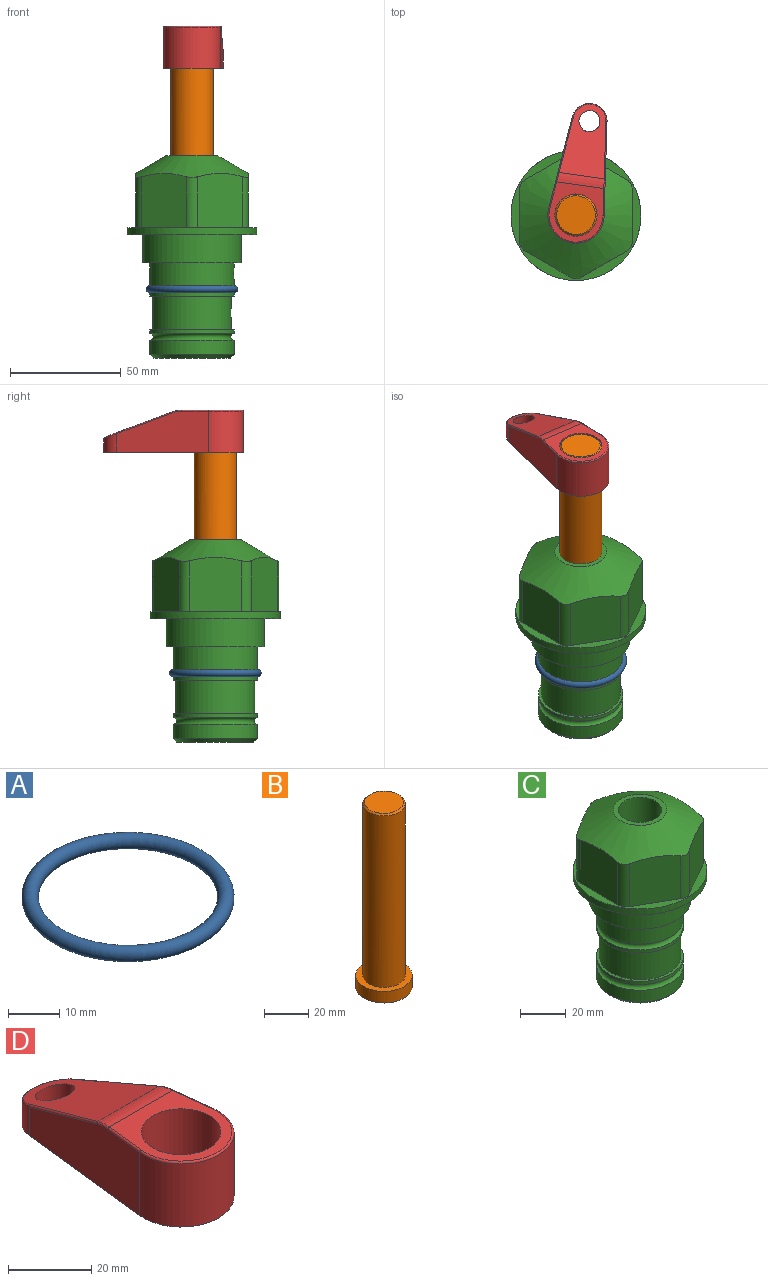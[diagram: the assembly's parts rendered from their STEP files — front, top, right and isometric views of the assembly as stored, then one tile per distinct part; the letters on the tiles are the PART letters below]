
ASSEMBLY  parts=4 mates=2
PART A: 1 faces, bbox 44.7x44.7x3.2 mm
  f0: torus R=19.05mm, axis (0,0,1), area 1193.9mm2
PART B: 6 faces, bbox 25.4x25.4x101.6 mm
  f0: plane 17.46x17.46mm, normal (0,0,1), area 239.5mm2, adj f5
  f1: plane 25.4x25.4mm, normal (0,0,-1), area 506.7mm2, adj f2
  f2: cylinder r=12.7mm len=25.4mm, axis (0,0,1), area 506.7mm2, adj f1,f3
  f3: plane 25.4x25.4mm, normal (0,0,1), area 221.7mm2, adj f2,f4
  f4: cylinder r=9.53mm len=94.46mm, axis (0,0,1), area 5653mm2, adj f3,f5
  f5: cone r=8.73mm half-angle=45deg, axis (0,0,-1), area 64.4mm2, adj f0,f4
PART C: 36 faces, bbox 58.7x58.7x91.2 mm
  f0: cylinder r=17.78mm len=35.56mm, axis (0,0,1), area 1670.8mm2, adj f23,f24,f31
  f1: cylinder r=19.05mm len=38.1mm, axis (0,0,1), area 1191.9mm2, adj f26,f27,f30
  f2: plane 58.66x58.66mm, normal (0,0,-1), area 1150.6mm2, adj f3,f28
  f3: cylinder r=29.33mm len=58.66mm, axis (0,0,-1), area 585.1mm2, adj f2,f4
  f4: plane 58.66x58.66mm, normal (0,0,1), area 475.9mm2, adj f3,f5,f6,f7,f8,f9,f10,f11
  f5: plane 24.5x20.32mm, normal (-0.5,0.87,0), area 562.8mm2, adj f4,f15,f16,f17
  f6: plane 24.5x20.32mm, normal (0.5,0.87,0), area 562.8mm2, adj f4,f14,f15,f17
  f7: plane 24.5x23.48mm, normal (1,0,0), area 562.8mm2, adj f4,f13,f14,f17
  f8: plane 24.5x20.32mm, normal (0.5,-0.87,0), area 562.8mm2, adj f4,f12,f13,f17
  f9: plane 24.5x20.32mm, normal (-0.5,-0.87,0), area 562.8mm2, adj f4,f11,f12,f17
  f10: plane 24.5x23.48mm, normal (-1,0,0), area 562.8mm2, adj f4,f11,f16,f17
  f11: cylinder r=5.08mm len=23.01mm, axis (0,0,-1), area 121.2mm2, adj f4,f9,f10,f17
  f12: cylinder r=5.08mm len=23.01mm, axis (0,0,-1), area 121.2mm2, adj f4,f8,f9,f17
  f13: cylinder r=5.08mm len=23.01mm, axis (0,0,-1), area 121.2mm2, adj f4,f7,f8,f17
  f14: cylinder r=5.08mm len=23.01mm, axis (0,0,-1), area 121.2mm2, adj f4,f6,f7,f17
  f15: cylinder r=5.08mm len=23.01mm, axis (0,0,-1), area 121.2mm2, adj f4,f5,f6,f17
  f16: cylinder r=5.08mm len=23.01mm, axis (0,0,-1), area 121.2mm2, adj f4,f5,f10,f17
  f17: cone r=11.73mm half-angle=60deg, axis (0,0,-1), area 2071.8mm2, adj f5,f6,f7,f8,f9,f10,f11,f12
  f18: plane 23.46x23.46mm, normal (0,0,1), area 147.4mm2, adj f17,f35
  f19: plane 34.93x34.93mm, normal (0,0,-1), area 958mm2, adj f29
  f20: cylinder r=19.05mm len=38.1mm, axis (0,0,1), area 760.1mm2, adj f21,f29
  f21: torus R=19.05mm, axis (0,0,1), area 565.3mm2, adj f20,f22
  f22: cylinder r=19.05mm len=38.1mm, axis (0,0,1), area 190mm2, adj f21,f23
  f23: plane 38.1x38.1mm, normal (0,0,1), area 146.9mm2, adj f0,f22
  f24: plane 38.1x38.1mm, normal (0,0,-1), area 146.9mm2, adj f0,f25
  f25: cylinder r=19.05mm len=38.1mm, axis (0,0,1), area 190mm2, adj f24,f26
  f26: torus R=19.05mm, axis (0,0,1), area 565.3mm2, adj f1,f25
  f27: plane 44.45x44.45mm, normal (0,0,-1), area 411.7mm2, adj f1,f28
  f28: cylinder r=22.23mm len=44.45mm, axis (0,0,1), area 1773.5mm2, adj f2,f27
  f29: cone r=19.05mm half-angle=45deg, axis (0,0,1), area 257.5mm2, adj f19,f20
  f30: cylinder r=3.17mm len=6.75mm, axis (-1,0,0), area 128mm2, adj f1,f33
  f31: cylinder r=3.17mm len=6.35mm, axis (-1,0,0), area 102.5mm2, adj f0,f33
  f32: plane 25.4x25.4mm, normal (0,0,1), area 506.7mm2, adj f33
  f33: cylinder r=12.7mm len=66.42mm, axis (0,0,-1), area 5236.2mm2, adj f30,f31,f32,f34
  f34: cone r=9.53mm half-angle=30deg, axis (0,0,-1), area 443.4mm2, adj f33,f35
  f35: cylinder r=9.53mm len=19.05mm, axis (0,0,-1), area 849mm2, adj f18,f34
PART D: 44 faces, bbox 27.5x64.5x19.1 mm
  f0: plane 2.3x0.95mm, normal (0,0,-1), area 1mm2, adj f25,f30,f34
  f1: plane 63.5x25.4mm, normal (0,0,-1), area 561.7mm2, adj f2,f3,f4,f5,f6,f7,f19,f20
  f2: cylinder r=12.7mm len=25.4mm, axis (0,0,-1), area 792.2mm2, adj f1,f3,f5,f13
  f3: plane 42.33x18.54mm, normal (0.99,0.11,0), area 647mm2, adj f1,f2,f4,f11,f12,f14
  f4: cylinder r=7.94mm len=15.78mm, axis (0,0,-1), area 158.6mm2, adj f1,f3,f5,f16
  f5: plane 42.33x18.54mm, normal (-0.99,0.11,0), area 647mm2, adj f1,f2,f4,f15,f17,f18
  f6: cylinder r=9.53mm len=19.05mm, axis (0,0,-1), area 1140.1mm2, adj f1,f8
  f7: cylinder r=4.76mm len=10.98mm, axis (0,0,-1), area 276.1mm2, adj f1,f9
  f8: plane 25.83x24.38mm, normal (0,0,1), area 262.2mm2, adj f6,f10,f11,f13,f15
  f9: plane 32.49x20.55mm, normal (0,0.34,0.94), area 489.9mm2, adj f7,f10,f14,f16,f18
  f10: cylinder r=12.7mm len=21.49mm, axis (-1,0,0), area 93.2mm2, adj f8,f9,f12,f17
  f11: cylinder r=0.51mm len=12.34mm, axis (0.11,-0.99,0), area 9.9mm2, adj f3,f8,f12,f13
  f12: bspline ~7.62x1.64mm, area 3.5mm2, adj f3,f10,f11,f14
  f13: torus R=12.19mm, axis (0,0,1), area 33.6mm2, adj f2,f8,f11,f15
  f14: cylinder r=0.51mm len=26.01mm, axis (0.1,-0.93,0.34), area 21.6mm2, adj f3,f9,f12,f16
  f15: cylinder r=0.51mm len=12.34mm, axis (0.11,0.99,0), area 9.9mm2, adj f5,f8,f13,f17
  f16: bspline ~15.78x7.05mm, area 15.7mm2, adj f4,f9,f14,f18
  f17: bspline ~7.62x1.64mm, area 3.5mm2, adj f5,f10,f15,f18
  f18: cylinder r=0.51mm len=26.01mm, axis (0.1,0.93,-0.34), area 21.6mm2, adj f5,f9,f16,f17
  f19: plane 21.6x14.29mm, normal (-0.99,-0.11,0), area 242.6mm2, adj f1,f26,f28,f34,f36,f38
  f20: plane 21.6x14.29mm, normal (0.99,-0.11,0), area 242.6mm2, adj f1,f27,f29,f37,f39,f41
  f21: cylinder r=12.7mm len=14.29mm, axis (0,0,-1), area 173.2mm2, adj f1,f26,f27,f30,f31,f33
  f22: cylinder r=7.94mm len=7.63mm, axis (0,0,-1), area 53.8mm2, adj f1,f28,f29,f42
  f23: plane 2.3x0.95mm, normal (0,0,-1), area 1mm2, adj f25,f33,f37
  f24: plane 17.94x12.32mm, normal (0,-0.34,-0.94), area 191.2mm2, adj f25,f38,f41,f42
  f25: cylinder r=9.53mm len=12.93mm, axis (-1,0,0), area 37.5mm2, adj f0,f23,f24,f31,f36,f39
  f26: cylinder r=1.59mm len=14.29mm, axis (0,0,-1), area 49mm2, adj f1,f19,f21,f32
  f27: cylinder r=1.59mm len=14.29mm, axis (0,0,-1), area 49mm2, adj f1,f20,f21,f35
  f28: cylinder r=1.59mm len=7.28mm, axis (0,0,-1), area 22.1mm2, adj f1,f19,f22,f40
  f29: cylinder r=1.59mm len=7.28mm, axis (0,0,-1), area 22.1mm2, adj f1,f20,f22,f43
  f30: torus R=14.29mm, axis (0,0,1), area 5.8mm2, adj f0,f21,f31,f32
  f31: bspline ~11.06x2.73mm, area 20.8mm2, adj f21,f25,f30,f33
  f32: sphere r=1.59mm, area 5.4mm2, adj f26,f30,f34
  f33: torus R=14.29mm, axis (0,0,1), area 5.8mm2, adj f21,f23,f31,f35
  f34: cylinder r=1.59mm len=1.68mm, axis (-0.11,0.99,0), area 2.4mm2, adj f0,f19,f32,f36
  f35: sphere r=1.59mm, area 5.4mm2, adj f27,f33,f37
  f36: bspline ~5.82x2.33mm, area 7.7mm2, adj f19,f25,f34,f38
  f37: cylinder r=1.59mm len=1.68mm, axis (0.11,0.99,0), area 2.4mm2, adj f20,f23,f35,f39
  f38: cylinder r=1.59mm len=18.33mm, axis (0.1,-0.93,0.34), area 46.7mm2, adj f19,f24,f36,f40
  f39: bspline ~5.82x2.33mm, area 7.7mm2, adj f20,f25,f37,f41
  f40: sphere r=1.59mm, area 3.6mm2, adj f28,f38,f42
  f41: cylinder r=1.59mm len=18.33mm, axis (0.1,0.93,-0.34), area 46.7mm2, adj f20,f24,f39,f43
  f42: bspline ~8.31x1.84mm, area 15.3mm2, adj f22,f24,f40,f43
  f43: sphere r=1.59mm, area 3.6mm2, adj f29,f41,f42
PLACE A at identity
PLACE B rot(axis=(0,0,-1),8.2deg) t=(0,0,20.51)mm
PLACE C at identity fixed
PLACE D rot(axis=(0,0,-1),8.2deg) t=(0,0,75.12)mm
MATE fastened D.f2 <-> B.f2  axis (0,0,-1) through (0,0,94.17)mm
MATE cylindrical B.f2 <-> C.f0  axis (0,0,1) through (0,0,46.15)mm
